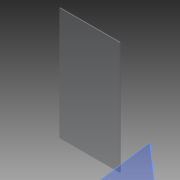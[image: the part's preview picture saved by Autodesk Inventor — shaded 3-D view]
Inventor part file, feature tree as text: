
AUTODESK INVENTOR PART (.ipt)
format: ipt  version: 2014 (Build 180170000, 170)  size: 101,376 bytes
history: native  units: in
note: dims shown in document units (in); Inventor stores cm internally (conversion verified against a paired STEP export)
features: extrude x1, sketch x1
ambient origin geometry x8: Origin, YZ Plane, XZ Plane, XY Plane, X Axis, Y Axis, Z Axis, Center Point
bodies: Solid1 (feature_tree)
feature tree (2):
  extrude  "Extrusion1"  Depth=15.0in
  sketch  "Sketch1"  dims[d0=8.0in d1=15.0in d2=0.125in d3=0.0in d4=1.0in d5=1.125in d6=1.25in d7=1.5in d8=3.125in d9=1.125in d10=1.0in d11=1.125in d12=1.25in d13=1.5in d14=1.25in d15=1.125in d16=1.125in]
